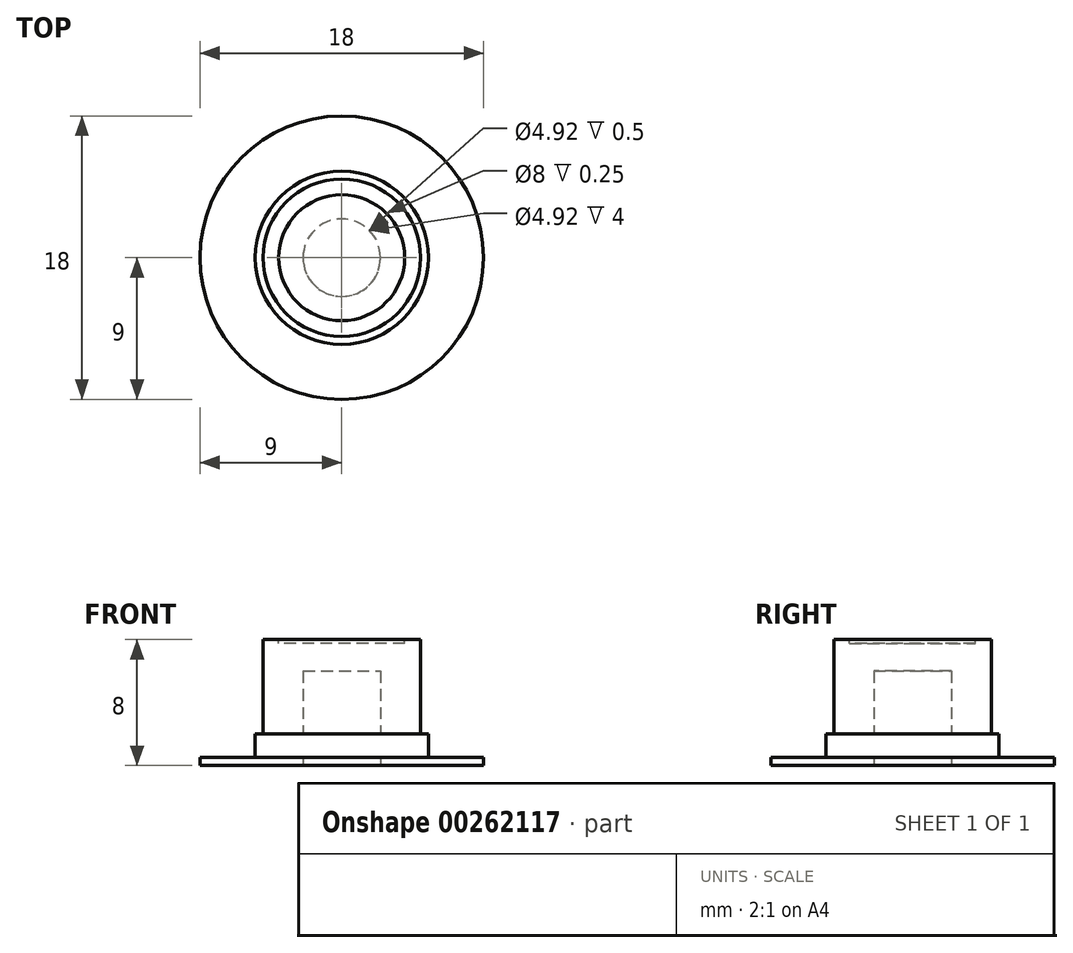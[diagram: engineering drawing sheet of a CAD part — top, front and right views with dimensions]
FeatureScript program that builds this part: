
annotation { "Feature Type Name" : "Feature", "Feature Type Description" : "" }
export const myFeature = defineFeature(function(context is Context, id is Id, definition is map)
    precondition{}
    {
        {
            var Q0;
            Q0=qCreatedBy(makeId("Top.planeOp"),FACE);
            var sketch = newSketch(context, id + "F0", { "sketchPlane" : qUnion([Q0])});
            skCircle(sketch, "E0", {"center": v(0, 0) * mm, "radius": 9 * mm});
            skSolve(sketch);
        }
        {
            var Q0;
            Q0 = qSketchRegion(id + "F0", true);
            extrude(context, id + "F1", {"entities" : qUnion([Q0]), "depth" : .5 * mm});
        }
        {
            var Q0;
            Q0=makeQuery(id+"F1.opExtrude","CAP_FACE",FACE,{"disambiguationData":[OSD([sQuery(id+"F0.wireOp",EDGE,"E0")])],"isStart":false});
            var sketch = newSketch(context, id + "F2", { "sketchPlane" : qUnion([Q0])});
            skCircle(sketch, "E1", {"center": v(0, 0) * mm, "radius": 5 * mm});
            skSolve(sketch);
        }
        {
            var Q0;
            Q0=makeQuery(id+"F2.imprint","IMPRINT",FACE,{"disambiguationData":[TD([[makeQuery(id+"F2.imprint","IMPRINT",EDGE,{"derivedFrom":sQuery(id+"F2.wireOp",EDGE,"E1")}),1.0]])]});
            extrude(context, id + "F3", {"entities" : qUnion([Q0]), "operationType" : NewBodyOperationType.ADD, "depth" : 8 * mm});
        }
        {
            var Q0;
            Q0=makeQuery(id+"F1.opExtrude","CAP_FACE",FACE,{"disambiguationData":[OSD([sQuery(id+"F0.wireOp",EDGE,"E0")])],"isStart":true});
            var sketch = newSketch(context, id + "F4", { "sketchPlane" : qUnion([Q0])});
            skCircle(sketch, "E2", {"center": v(0, 0) * mm, "radius": 2.46 * mm});
            skSolve(sketch);
        }
        {
            var Q0;
            Q0 = qSketchRegion(id + "F4", true);
            extrude(context, id + "F5", {"entities" : qUnion([Q0]), "operationType" : NewBodyOperationType.REMOVE, "oppositeDirection" : true, "depth" : 6 * mm});
        }
        {
            var Q0;
            Q0=makeQuery(id+"F3.opExtrude","CAP_FACE",FACE,{"disambiguationData":[OSD([sQuery(id+"F2.wireOp",EDGE,"E1")])],"isStart":false});
            var sketch = newSketch(context, id + "F6", { "sketchPlane" : qUnion([Q0])});
            skCircle(sketch, "E3", {"center": v(0, 0) * mm, "radius": 5 * mm});
            skSolve(sketch);
        }
        {
            var Q0;
            Q0=makeQuery(id+"F6.imprint","IMPRINT",FACE,{"disambiguationData":[TD([[makeQuery(id+"F6.imprint","IMPRINT",EDGE,{"derivedFrom":sQuery(id+"F6.wireOp",EDGE,"E3")}),1.0]])]});
            extrude(context, id + "F7", {"entities" : qUnion([Q0]), "operationType" : NewBodyOperationType.REMOVE, "oppositeDirection" : true, "depth" : .5 * mm});
        }
        {
            var Q0;
            Q0=makeQuery(id+"F1.opExtrude","CAP_FACE",FACE,{"disambiguationData":[OSD([sQuery(id+"F0.wireOp",EDGE,"E0")])],"isStart":false});
            var sketch = newSketch(context, id + "F8", { "sketchPlane" : qUnion([Q0])});
            skCircle(sketch, "E4", {"center": v(0, 0) * mm, "radius": 5.5 * mm});
            skSolve(sketch);
        }
        {
            var Q0;
            Q0 = qSketchRegion(id + "F8", true);
            extrude(context, id + "F9", {"entities" : qUnion([Q0]), "operationType" : NewBodyOperationType.ADD, "depth" : 1.5 * mm});
        }
        {
            var Q0;
            Q0=makeQuery(id+"F7.boolean.opBoolean","COPY",FACE,{"derivedFrom":makeQuery(id+"F7.opExtrude","CAP_FACE",FACE,{"disambiguationData":[OSD([sQuery(id+"F6.wireOp",EDGE,"E3")])],"isStart":false})});
            var sketch = newSketch(context, id + "F10", { "sketchPlane" : qUnion([Q0])});
            skCircle(sketch, "E5", {"center": v(0, 0) * mm, "radius": 4 * mm});
            skSolve(sketch);
        }
        {
            var Q0;
            Q0=makeQuery(id+"F10.imprint","IMPRINT",FACE,{"disambiguationData":[TD([[makeQuery(id+"F10.imprint","IMPRINT",EDGE,{"derivedFrom":sQuery(id+"F10.wireOp",EDGE,"E5")}),1.0]])]});
            extrude(context, id + "F11", {"entities" : qUnion([Q0]), "operationType" : NewBodyOperationType.REMOVE, "oppositeDirection" : true, "depth" : .25 * mm});
        }
    });
